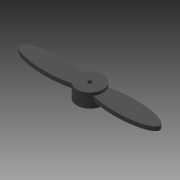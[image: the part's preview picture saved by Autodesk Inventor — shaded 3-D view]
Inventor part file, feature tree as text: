
AUTODESK INVENTOR PART (.ipt)
format: ipt  version: 2015 (Build 190159000, 159)  size: 100,864 bytes
history: native  units: mm
features: extrude x5, sketch x2
ambient origin geometry x8: Origin, YZ Plane, XZ Plane, XY Plane, X Axis, Y Axis, Z Axis, Center Point
bodies: Solid1 (feature_tree)
feature tree (7):
  sketch  "Sketch1"  dims[d0=13.0mm d1=17.3675mm]
  extrude  "Extrusion1"  Depth=17.3675mm
  extrude  "Extrusion2"  Depth=6.93mm TaperAngle=0.0deg
  extrude  "Extrusion3"  Depth=2.0mm TaperAngle=0.0deg
  extrude  "Extrusion4"  Depth=2.0mm
  extrude  "Extrusion5"  Depth=2.0mm TaperAngle=0.0deg
  sketch  "Sketch2"  dims[d2=5.08mm d3=6.93mm d4=0.0mm d5=2.0mm d6=0.0mm d7=2.0mm d8=2.0mm d9=0.0mm d10=1.0mm d11=0.0mm d12=2.0mm d13=0.0mm]
